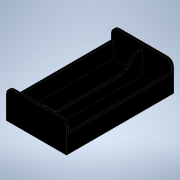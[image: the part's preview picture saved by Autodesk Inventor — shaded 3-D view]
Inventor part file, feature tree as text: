
AUTODESK INVENTOR PART (.ipt)
format: ipt  version: 2020 (Build 240168000, 168)  size: 196,608 bytes
history: native  units: mm
features: extrude x8, sketch x8, fillet x5, chamfer x2, plane x1
ambient origin geometry x8: Origin, YZ Plane, XZ Plane, XY Plane, X Axis, Y Axis, Z Axis, Center Point
bodies: Solid1 (feature_tree)
feature tree (24):
  extrude  "Extrusion1"  Depth=20.0mm
  fillet  "Fillet1"  Radius=1.5mm
  extrude  "Extrusion2"  Depth=1.5mm
  extrude  "Extrusion3"  Depth=70.0mm TaperAngle=0.0deg
  extrude  "Extrusion4"  Depth=12.0mm
  fillet  "Fillet2"  Radius=70.0mm
  extrude  "Extrusion5"  Depth=4.0mm
  plane  "Work Plane1"
  extrude  "Extrusion6"  [1 undecoded]
  chamfer  "Chamfer1"  Distance=1.5mm
  fillet  "Fillet3"  Radius=4.0mm
  extrude  "Extrusion7"  Depth=15.0mm
  chamfer  "Chamfer2"  Distance=12.0mm
  fillet  "Fillet4"  Radius=15.0mm
  extrude  "Extrusion8"  Depth=1.5mm TaperAngle=0.0deg
  fillet  "Fillet5"  Radius=8.0mm
  sketch  "Sketch1"  dims[d0=41.0mm d1=20.0mm d2=1.5mm d3=0.0mm]
  sketch  "Sketch3"  dims[d4=4.0mm d5=1.5mm]
  sketch  "Sketch4"  dims[d6=12.0mm d7=70.0mm d8=0.0mm]
  sketch  "Sketch5"  dims[d9=1.5mm d10=12.0mm d11=70.0mm d12=0.0mm]
  sketch  "Sketch6"  dims[d13=1.5mm d14=0.0mm d15=4.0mm]
  sketch  "Sketch9"  dims[d16=1.5mm d17=0.0mm d18=-20.5mm d19=1.5mm d20=0.0mm]
  sketch  "Sketch10"  dims[d21=8.0mm d22=2.0mm d23=45.0deg d24=4.0mm]
  sketch  "Sketch11"  dims[d25=12.0mm d26=15.0mm d27=12.0mm d28=15.0mm d29=1.5mm d30=0.0mm d31=8.0mm d32=2.0mm d33=45.0deg d34=4.0mm d35=50.0mm d36=0.0mm d37=6.0mm]
note: 1 required parameter value undecoded (feature->parameter linkage not recoverable at this tier; creation-order binding heuristic only, values carry confidence <= 0.55)
